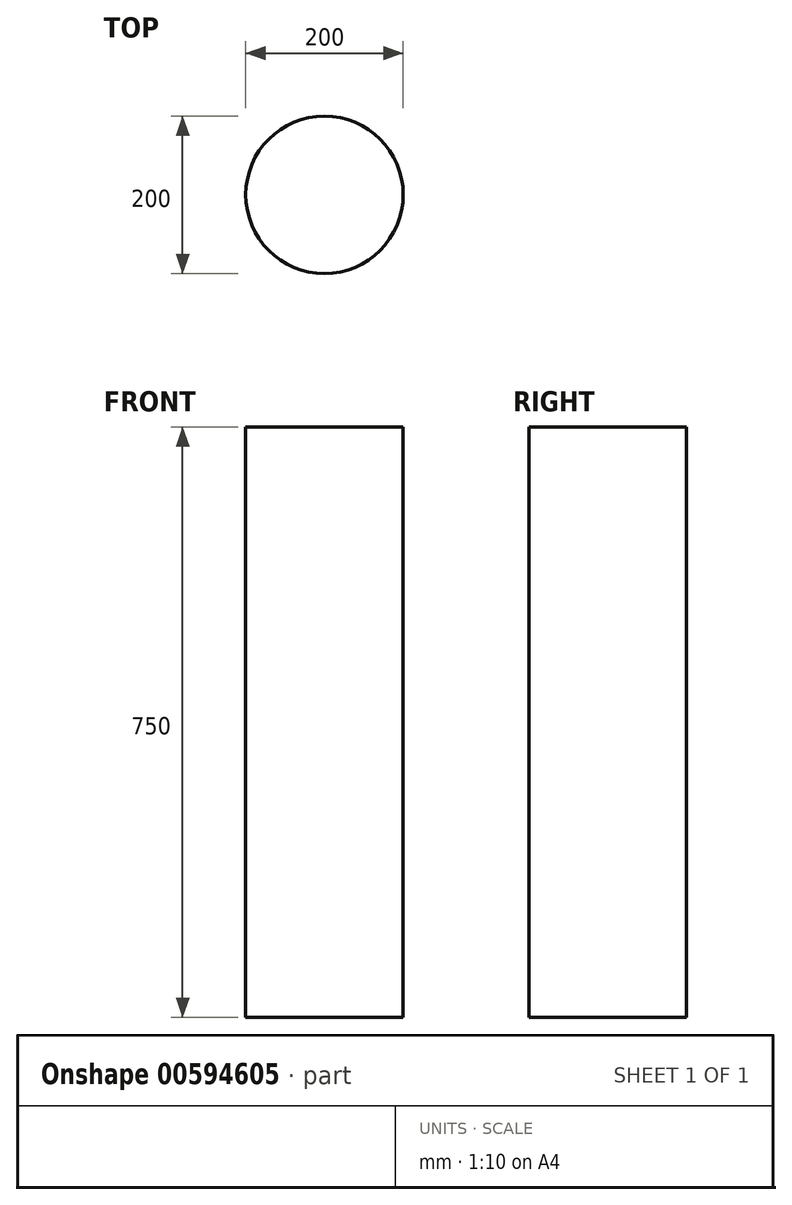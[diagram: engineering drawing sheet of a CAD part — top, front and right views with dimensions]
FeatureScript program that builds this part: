
annotation { "Feature Type Name" : "Feature", "Feature Type Description" : "" }
export const myFeature = defineFeature(function(context is Context, id is Id, definition is map)
    precondition{}
    {
        {
            var Q0;
            Q0=qCreatedBy(makeId("Top.planeOp"),FACE);
            var sketch = newSketch(context, id + "F0", { "sketchPlane" : qUnion([Q0])});
            skCircle(sketch, "E0", {"center": v(0, 0) * mm, "radius": 100 * mm});
            skSolve(sketch);
        }
        {
            var Q0;
            Q0 = qSketchRegion(id + "F0", true);
            extrude(context, id + "F1", {"entities" : qUnion([Q0]), "depth" : 750 * mm, "offsetDistance" : 25 * mm});
        }
    });
